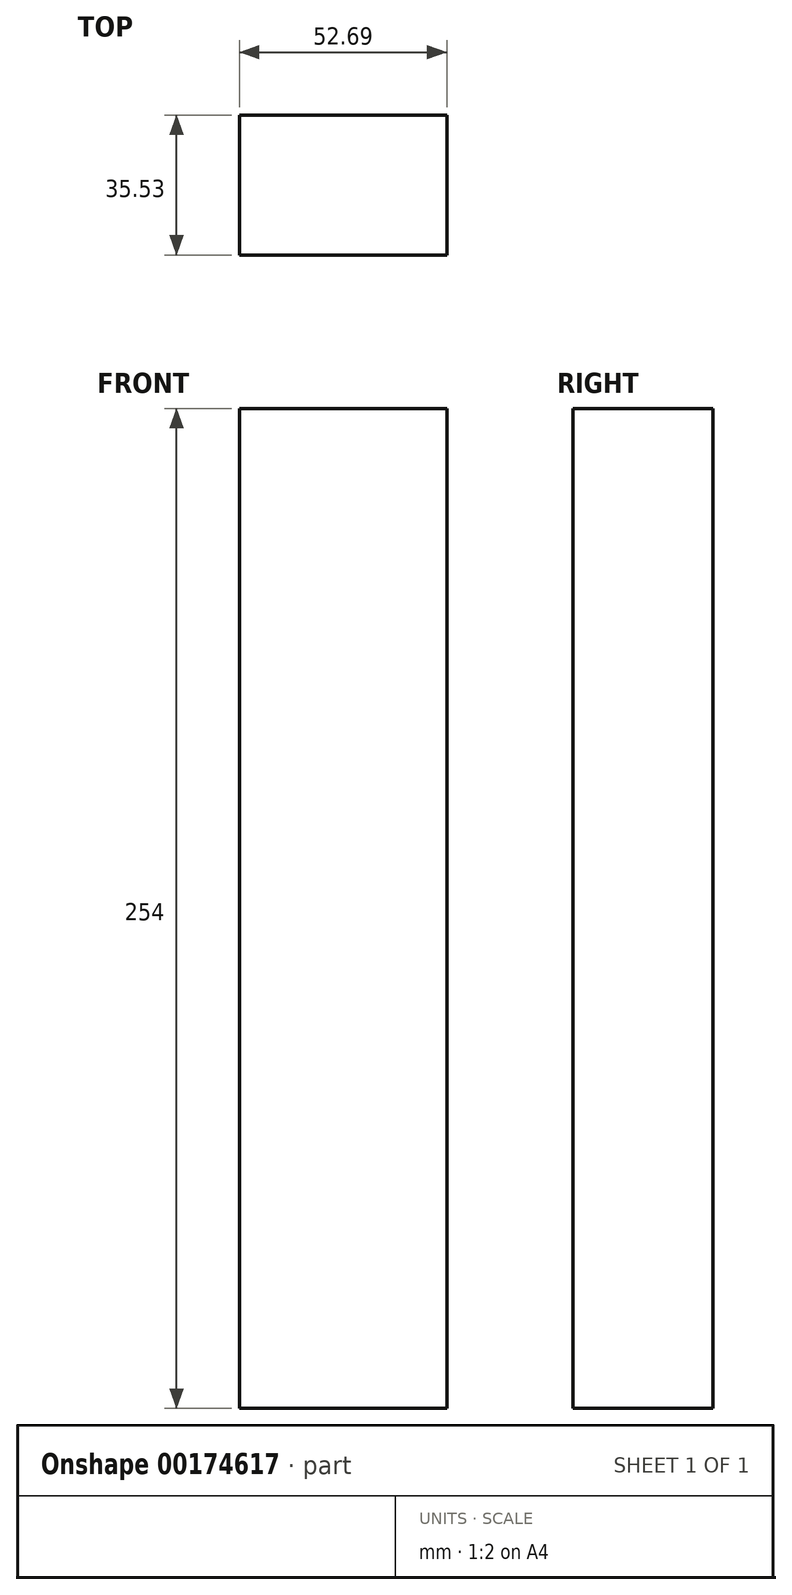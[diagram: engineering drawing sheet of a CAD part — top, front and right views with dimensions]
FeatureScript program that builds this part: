
annotation { "Feature Type Name" : "Feature", "Feature Type Description" : "" }
export const myFeature = defineFeature(function(context is Context, id is Id, definition is map)
    precondition{}
    {
        {
            var Q0;
            Q0=qCreatedBy(makeId("Top.planeOp"),FACE);
            var sketch = newSketch(context, id + "F0", { "sketchPlane" : qUnion([Q0])});
            skCircle(sketch, "E0", {"center": v(-47.95, -6.31) * mm, "radius": 24.75 * mm});
            skLineSegment(sketch, "E1.bottom", {"start": v(52.7, 35.53) * mm, "end": v(0, 35.53) * mm});
            skLineSegment(sketch, "E1.top", {"start": v(52.7, 0) * mm, "end": v(0, 0) * mm});
            skLineSegment(sketch, "E1.left", {"start": v(52.7, 35.53) * mm, "end": v(52.7, 0) * mm});
            skLineSegment(sketch, "E1.right", {"start": v(0, 35.53) * mm, "end": v(0, 0) * mm});
            skSolve(sketch);
        }
        {
            var Q0;
            Q0=makeQuery(id+"F0.imprint","IMPRINT",FACE,{"disambiguationData":[TD([[makeQuery(id+"F0.imprint","IMPRINT",EDGE,{"derivedFrom":sQuery(id+"F0.wireOp",EDGE,"E1.bottom")}),1.0]])]});
            extrude(context, id + "F1", {"entities" : qUnion([Q0]), "depth" : 254 * mm});
        }
    });
